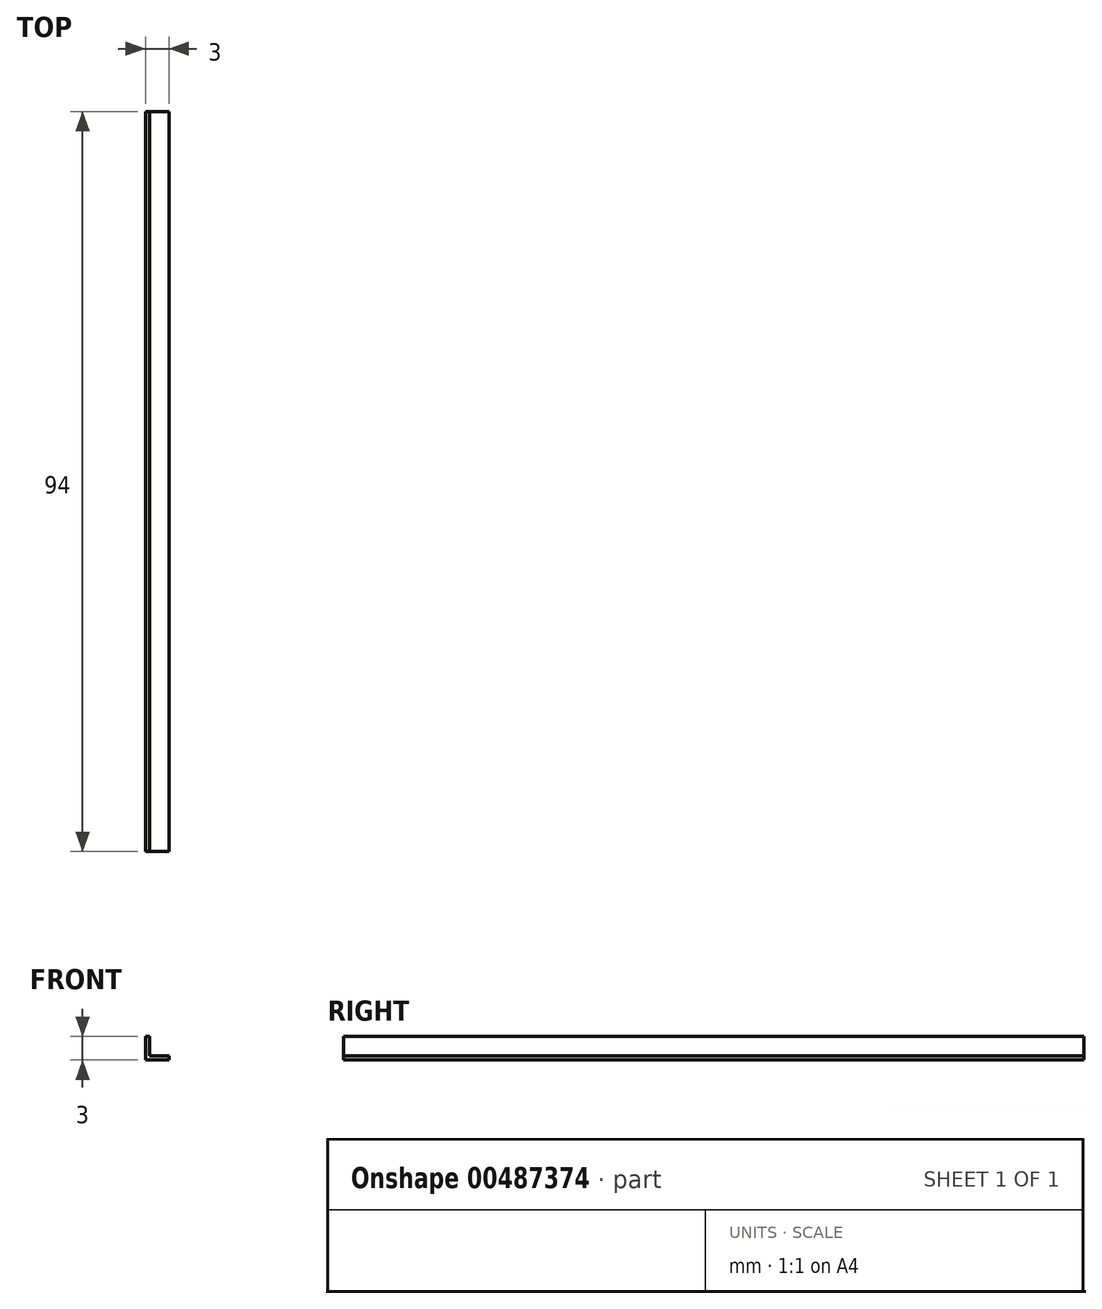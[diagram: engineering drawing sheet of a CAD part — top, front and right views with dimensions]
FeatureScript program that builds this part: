
annotation { "Feature Type Name" : "Feature", "Feature Type Description" : "" }
export const myFeature = defineFeature(function(context is Context, id is Id, definition is map)
    precondition{}
    {
        {
            var Q0;
            Q0=qCreatedBy(makeId("Front.planeOp"),FACE);
            var sketch = newSketch(context, id + "F0", { "sketchPlane" : qUnion([Q0])});
            skLineSegment(sketch, "E0", {"start": v(0, 3) * mm, "end": v(0, 0) * mm});
            skLineSegment(sketch, "E1", {"start": v(0, 0) * mm, "end": v(3, 0) * mm});
            skLineSegment(sketch, "E2", {"start": v(3, 0) * mm, "end": v(3, 0.5) * mm});
            skLineSegment(sketch, "E3", {"start": v(3, 0.5) * mm, "end": v(0.5, 0.5) * mm});
            skLineSegment(sketch, "E4", {"start": v(0.5, 0.5) * mm, "end": v(0.5, 3) * mm});
            skLineSegment(sketch, "E5", {"start": v(0.5, 3) * mm, "end": v(0, 3) * mm});
            skSolve(sketch);
        }
        {
            var Q0;
            Q0 = qSketchRegion(id + "F0", true);
            extrude(context, id + "F1", {"entities" : qUnion([Q0]), "depth" : 94 * mm});
        }
    });
